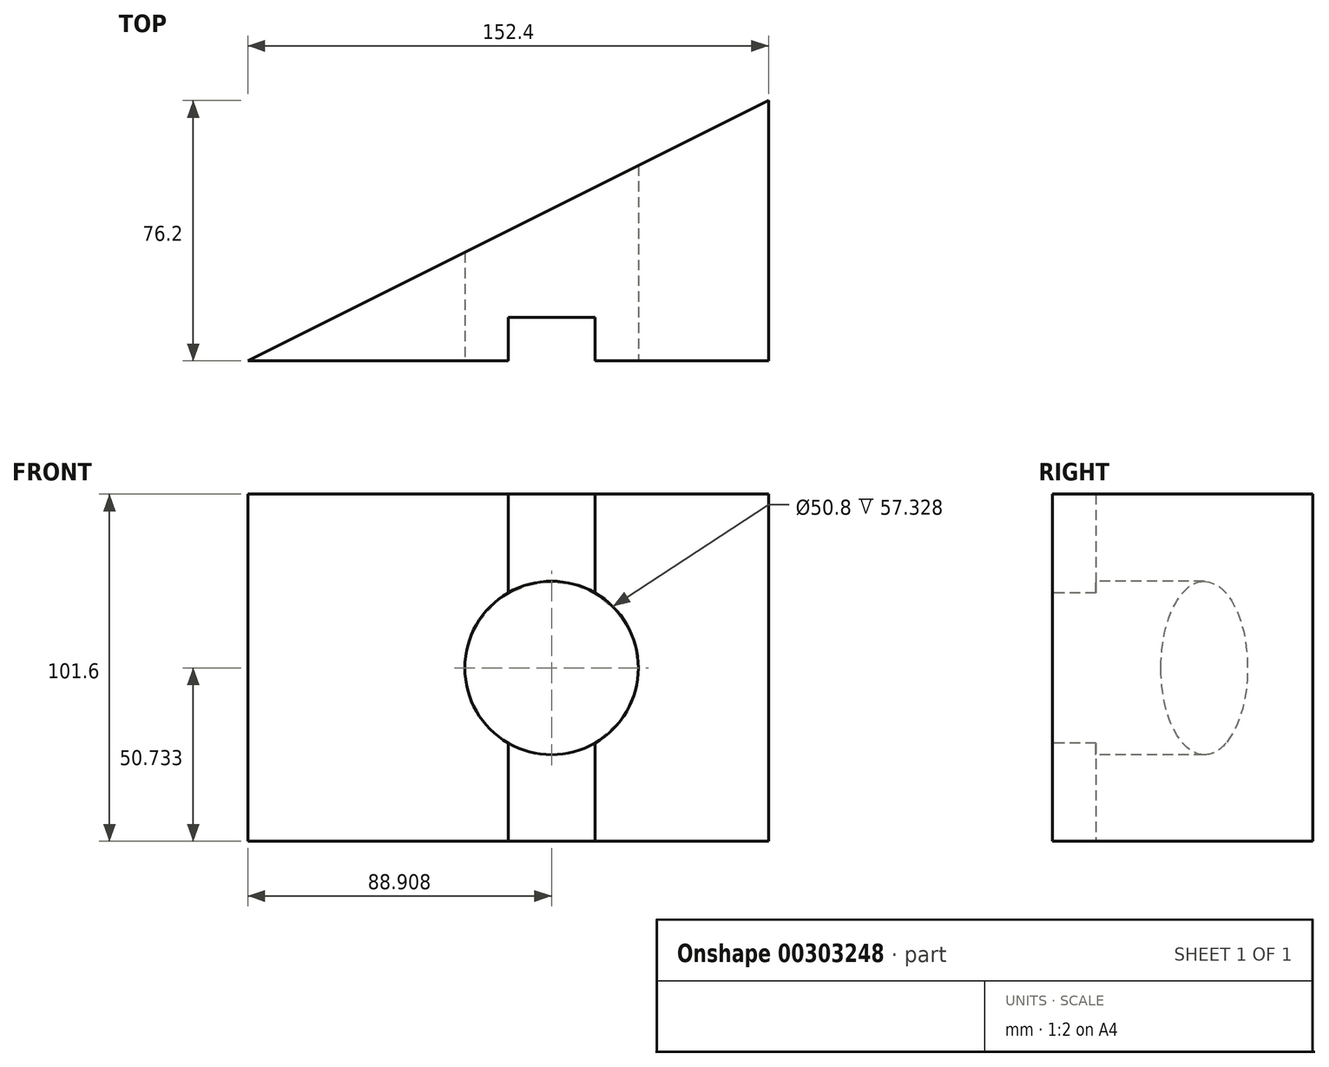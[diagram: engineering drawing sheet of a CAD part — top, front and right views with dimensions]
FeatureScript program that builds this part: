
annotation { "Feature Type Name" : "Feature", "Feature Type Description" : "" }
export const myFeature = defineFeature(function(context is Context, id is Id, definition is map)
    precondition{}
    {
        {
            var Q0;
            Q0=qCreatedBy(makeId("Top.planeOp"),FACE);
            var sketch = newSketch(context, id + "F0", { "sketchPlane" : qUnion([Q0])});
            skLineSegment(sketch, "E0.bottom", {"start": v(0, 0) * mm, "end": v(152.4, 0) * mm});
            skLineSegment(sketch, "E0.top", {"start": v(0, 76.2) * mm, "end": v(152.4, 76.2) * mm});
            skLineSegment(sketch, "E0.left", {"start": v(0, 0) * mm, "end": v(0, 76.2) * mm});
            skLineSegment(sketch, "E0.right", {"start": v(152.4, 0) * mm, "end": v(152.4, 76.2) * mm});
            skLineSegment(sketch, "E1", {"start": v(0, 0) * mm, "end": v(152.4, 76.2) * mm});
            skSolve(sketch);
        }
        {
            var Q0;
            Q0=makeQuery(id+"F0.imprint","IMPRINT",FACE,{"disambiguationData":[TD([[makeQuery(id+"F0.imprint","IMPRINT",EDGE,{"derivedFrom":sQuery(id+"F0.wireOp",EDGE,"E0.bottom")}),1.0]])]});
            extrude(context, id + "F1", {"entities" : qUnion([Q0]), "depth" : 101.6 * mm});
        }
        {
            var Q0;
            Q0=makeQuery(id+"F1.opExtrude","SWEPT_FACE",FACE,{"disambiguationData":[OSD([sQuery(id+"F0.wireOp",EDGE,"E0.bottom")])]});
            var sketch = newSketch(context, id + "F2", { "sketchPlane" : qUnion([Q0])});
            skSolve(sketch);
        }
        {
            var Q0;
            {var subQ0=sQuery(id+"F0.wireOp",EDGE,"E0.bottom");Q0=makeQuery(id+"F2.imprint","IMPRINT",FACE,{"disambiguationData":[TD([[makeQuery(id+"F2.imprint","IMPRINT",EDGE,{"derivedFrom":makeQuery(id+"F1.opExtrude","CAP_EDGE",EDGE,{"disambiguationData":[OSD([subQ0])],"isStart":true})}),1.0]])]});}
            var sketch = newSketch(context, id + "F3", { "sketchPlane" : qUnion([Q0])});
            skLineSegment(sketch, "E2.bottom", {"start": v(101.6, 101.6) * mm, "end": v(76.2, 101.6) * mm});
            skLineSegment(sketch, "E2.top", {"start": v(101.6, 0) * mm, "end": v(76.2, 0) * mm});
            skLineSegment(sketch, "E2.left", {"start": v(101.6, 101.6) * mm, "end": v(101.6, 0) * mm});
            skLineSegment(sketch, "E2.right", {"start": v(76.2, 101.6) * mm, "end": v(76.2, 0) * mm});
            skPoint(sketch, "E2.middle", {"position": v(88.9, 50.8) * mm});
            skSolve(sketch);
        }
        {
            var Q0;
            Q0=makeQuery(id+"F3.imprint","IMPRINT",FACE,{"disambiguationData":[TD([[makeQuery(id+"F3.imprint","IMPRINT",EDGE,{"derivedFrom":sQuery(id+"F3.wireOp",EDGE,"E2.bottom")}),-1.0]])]});
            extrude(context, id + "F4", {"entities" : qUnion([Q0]), "operationType" : NewBodyOperationType.REMOVE, "oppositeDirection" : true, "depth" : 12.7 * mm});
        }
        {
            var Q0;
            {var subQ0=sQuery(id+"F0.wireOp",EDGE,"E0.bottom");Q0=makeQuery(id+"F2.imprint","IMPRINT",FACE,{"disambiguationData":[TD([[makeQuery(id+"F2.imprint","IMPRINT",EDGE,{"derivedFrom":makeQuery(id+"F1.opExtrude","CAP_EDGE",EDGE,{"disambiguationData":[OSD([subQ0])],"isStart":true})}),1.0]])]});}
            var sketch = newSketch(context, id + "F5", { "sketchPlane" : qUnion([Q0])});
            skCircle(sketch, "E3", {"center": v(88.9, 50.73) * mm, "radius": 25.4 * mm});
            skSolve(sketch);
        }
        {
            var Q0;
            Q0=makeQuery(id+"F5.imprint","IMPRINT",FACE,{"disambiguationData":[TD([[makeQuery(id+"F5.imprint","IMPRINT",EDGE,{"derivedFrom":sQuery(id+"F5.wireOp",EDGE,"E3")}),1.0]])]});
            extrude(context, id + "F6", {"entities" : qUnion([Q0]), "operationType" : NewBodyOperationType.REMOVE, "endBound" : BoundingType.THROUGH_ALL, "oppositeDirection" : true, "depth" : 114.55 * mm});
        }
    });
